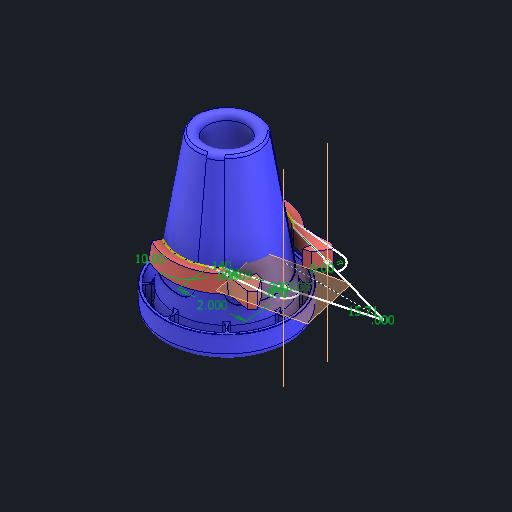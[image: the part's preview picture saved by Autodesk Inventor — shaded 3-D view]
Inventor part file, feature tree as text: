
AUTODESK INVENTOR PART (.ipt)
format: ipt  version: 2024.2 (Build 282272000, 272)  size: 3,192,320 bytes
history: native  units: in
note: dims shown in document units (in); Inventor stores cm internally (conversion verified against a paired STEP export)
features: other x10, sketch x8, reference x7, plane x5, extrude x4, projected_geometry x3, revolve x1, fillet x1
ambient origin geometry x8: Origin, YZ Plane, XZ Plane, XY Plane, X Axis, Y Axis, Z Axis, Center Point
bodies: Solid1 (feature_tree)
feature tree (39):
  other  "am-4801_Blue am-4801_Red Cone REV2.STEP"
  plane  "Work Plane2"
  sketch  "Sketch1"  dims[d1=1.0in d2=0.1in]
  plane  "Work Plane3"
  sketch  "Sketch2"  dims[d3=0.0in d4=30.0deg]
  sketch  "3D Sketch1"
  plane  "Work Plane4"
  revolve  "Revolution1"  [1 undecoded]
  extrude  "Extrusion1"  TaperAngle=30.0deg  [1 undecoded]
  extrude  "Extrusion2"  Depth=0.25in
  other  "Work Point1"
  other  "Work Point2"
  other  "Work Axis1"
  other  "Work Axis2"
  plane  "Work Plane5"
  extrude  "Extrusion3"  Depth=0.1in
  plane  "Work Plane6"
  extrude  "Extrusion4"  TaperAngle=240.0deg  [1 undecoded]
  projected_geometry  "Projected Loop1"
  projected_geometry  "Projected Loop2"
  sketch  "Sketch3"  dims[d5=30.0deg d7=0.25in]
  sketch  "Sketch4"  dims[d8=0.5in d9=0.1in]
  sketch  "Sketch5"  dims[d10=0.25in d11=240.0deg d12=0.0in]
  sketch  "Sketch6"  dims[d13=5.0in]
  sketch  "Sketch7"  dims[d14=1.0in d15=1.0in d16=0.0in d18=0.0687in d21=0.2in d22=0.0in d23=0.1397in d24=0.2091in d25=2.0in d26=0.0in d27=0.0in d28=0.0in d29=0.1079in d30=0.0in d31=0.85in d32=1.0in d33=0.0in d34=1.0in d35=0.0in d36=1.0in d37=0.0in d17=0.5in]
  reference  "Reference1"
  reference  "Reference2"
  reference  "Reference3"
  reference  "Reference4"
  reference  "Reference5"
  reference  "Reference6"
  reference  "Reference7"
  fillet  "Fillet23"  [1 undecoded]
  projected_geometry  "Project Cut Edges1"
  other  "<userpath>\Desktop\Robotics\Cad\Powerplay_Fun\Parts\Claw_Assembly.iam"
  other  "Claw_Assembly.iam"
  other  "Spur Gears:1"
  other  "Spur Gear2:1"
  other  "Spur Gear1:1"
note: 4 required parameter values undecoded (feature->parameter linkage not recoverable at this tier; creation-order binding heuristic only, values carry confidence <= 0.55)